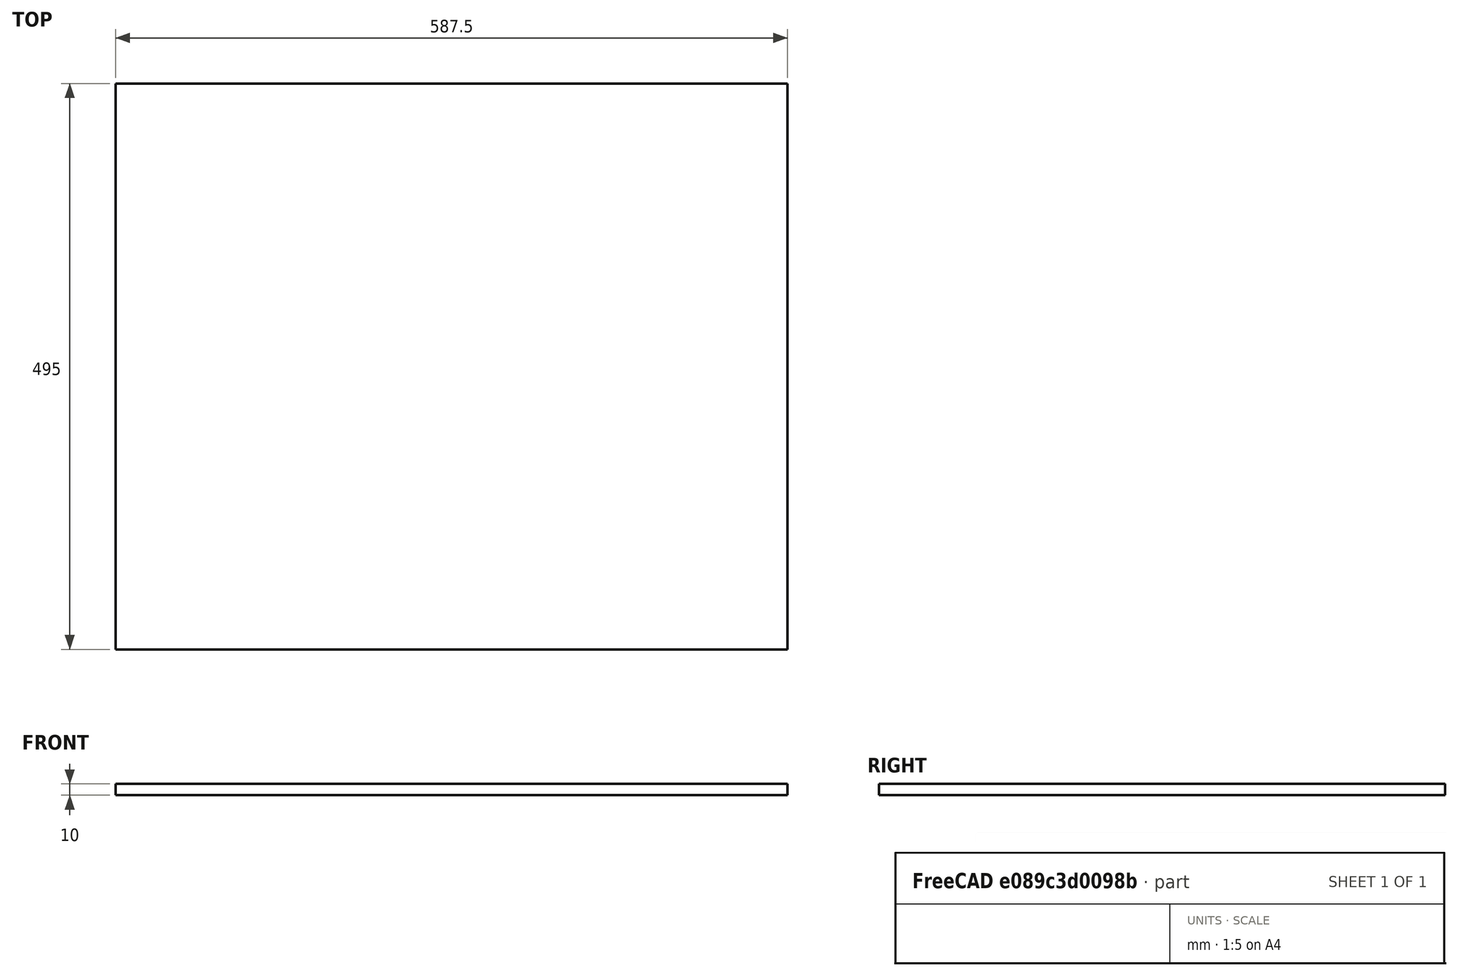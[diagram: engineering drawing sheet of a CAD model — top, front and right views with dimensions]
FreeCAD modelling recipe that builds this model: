
FCSTD DOCUMENT  (FreeCAD 1.0R39109 (Git))
Label: plate for controler
License: All rights reserved
LicenseURL: https://en.wikipedia.org/wiki/All_rights_reserved
objects: Sketcher::SketchObject×1, PartDesign::Pad×1, PartDesign::Body×1
note: 6 computed .brp shape members not serialized (recipe doc carries the construction recipe); baked Part::Feature solids carry a one-line shape summary decoded from their .brp

FEATURE [Sketcher::SketchObject] Sketch
  ArcFitTolerance = 1e-06
  AttachmentSupport = -> [XY_Plane]
  FullyConstrained = false
  MakeInternals = false
  MapMode = 5
  sketch-geometry (4):
    g0: LineSegment StartX=3156.83 StartY=26.2797 StartZ=0 EndX=3156.83 EndY=-468.72 EndZ=0
    g1: LineSegment StartX=3156.83 StartY=-468.72 StartZ=0 EndX=3744.33 EndY=-468.72 EndZ=0
    g2: LineSegment StartX=3744.33 StartY=-468.72 StartZ=0 EndX=3744.33 EndY=26.2797 EndZ=0
    g3: LineSegment StartX=3744.33 StartY=26.2797 StartZ=0 EndX=3156.83 EndY=26.2797 EndZ=0
  constraints (10):
    c: Coincident(g0,g1)
    c: Coincident(g1,g2)
    c: Coincident(g2,g3)
    c: Coincident(g3,g0)
    c: Vertical(g0)
    c: Vertical(g2)
    c: Horizontal(g1)
    c: Horizontal(g3)
    c: Distance(g0,g2) = 587.5
    c: Distance(g1,g3) = 495
FEATURE [PartDesign::Pad] Pad
  Direction = (0,0,1)
  Length = 10
  Length2 = 10
  Profile = -> Sketch
  ReferenceAxis = -> Sketch [N_Axis]
  Refine = true
  Suppressed = false
  Type = 0
FEATURE [PartDesign::Body] Body
  AllowCompound = false
  Group = -> [Sketch,Pad]
  Origin = -> Origin
  Tip = -> Pad
